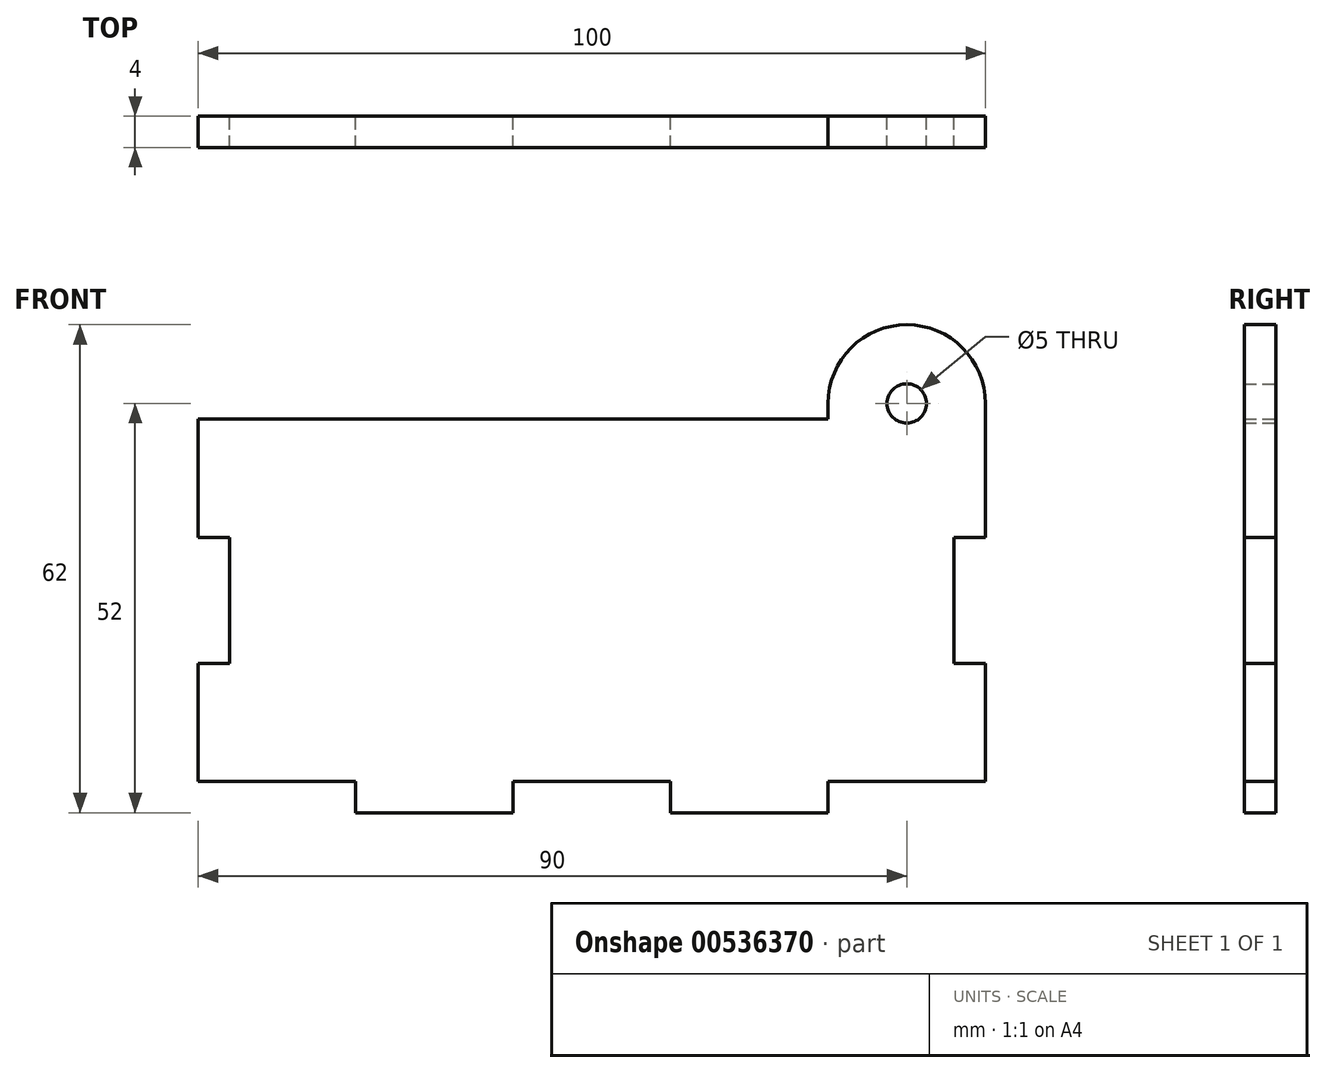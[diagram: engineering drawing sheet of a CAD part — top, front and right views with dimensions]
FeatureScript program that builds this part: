
annotation { "Feature Type Name" : "Feature", "Feature Type Description" : "" }
export const myFeature = defineFeature(function(context is Context, id is Id, definition is map)
    precondition{}
    {
        {
            var Q0;
            Q0=qCreatedBy(makeId("Front.planeOp"),FACE);
            var sketch = newSketch(context, id + "F0", { "sketchPlane" : qUnion([Q0])});
            skLineSegment(sketch, "E0.bottom", {"start": v(0, 0) * mm, "end": v(100, 0) * mm});
            skLineSegment(sketch, "E0.top", {"start": v(0, 50) * mm, "end": v(80, 50) * mm});
            skLineSegment(sketch, "E0.left", {"start": v(0, 0) * mm, "end": v(0, 50) * mm});
            skLineSegment(sketch, "E0.right", {"start": v(100, 0) * mm, "end": v(100, 50) * mm});
            skLineSegment(sketch, "E1.bottom", {"start": v(0, 0) * mm, "end": v(20, 0) * mm});
            skLineSegment(sketch, "E1.top", {"start": v(0, 4) * mm, "end": v(20, 4) * mm});
            skLineSegment(sketch, "E1.left", {"start": v(0, 0) * mm, "end": v(0, 4) * mm});
            skLineSegment(sketch, "E1.right", {"start": v(20, 0) * mm, "end": v(20, 4) * mm});
            skLineSegment(sketch, "E2.bottom", {"start": v(40, 0) * mm, "end": v(60, 0) * mm});
            skLineSegment(sketch, "E2.top", {"start": v(40, 4) * mm, "end": v(60, 4) * mm});
            skLineSegment(sketch, "E2.left", {"start": v(40, 0) * mm, "end": v(40, 4) * mm});
            skLineSegment(sketch, "E2.right", {"start": v(60, 0) * mm, "end": v(60, 4) * mm});
            skLineSegment(sketch, "E3.bottom", {"start": v(0, 35) * mm, "end": v(4, 35) * mm});
            skLineSegment(sketch, "E3.top", {"start": v(0, 19) * mm, "end": v(4, 19) * mm});
            skLineSegment(sketch, "E3.left", {"start": v(0, 35) * mm, "end": v(0, 19) * mm});
            skLineSegment(sketch, "E3.right", {"start": v(4, 35) * mm, "end": v(4, 19) * mm});
            skLineSegment(sketch, "E4.bottom", {"start": v(100, 35) * mm, "end": v(96, 35) * mm});
            skLineSegment(sketch, "E4.top", {"start": v(100, 19) * mm, "end": v(96, 19) * mm});
            skLineSegment(sketch, "E4.left", {"start": v(100, 35) * mm, "end": v(100, 19) * mm});
            skLineSegment(sketch, "E4.right", {"start": v(96, 35) * mm, "end": v(96, 19) * mm});
            skLineSegment(sketch, "E5.left", {"start": v(100, 50) * mm, "end": v(100, 52) * mm});
            skLineSegment(sketch, "E5.right", {"start": v(80, 50) * mm, "end": v(80, 52) * mm});
            skArc(sketch, "E6", {"start": v(100, 52) * mm, "mid": v(90, 62) * mm, "end": v(80, 52) * mm});
            skCircle(sketch, "E7", {"center": v(90, 52) * mm, "radius": 2.5 * mm});
            skLineSegment(sketch, "E8.bottom", {"start": v(100, 0) * mm, "end": v(80, 0) * mm});
            skLineSegment(sketch, "E8.top", {"start": v(100, 4) * mm, "end": v(80, 4) * mm});
            skLineSegment(sketch, "E8.left", {"start": v(100, 0) * mm, "end": v(100, 4) * mm});
            skLineSegment(sketch, "E8.right", {"start": v(80, 0) * mm, "end": v(80, 4) * mm});
            skSolve(sketch);
        }
        {
            var Q0;
            {var subQ2=sQuery(id+"F0.wireOp",EDGE,"E0.top");Q0=makeQuery(id+"F0.imprint","IMPRINT",FACE,{"disambiguationData":[TD([[makeQuery(id+"F0.imprint","IMPRINT",EDGE,{"derivedFrom":subQ2}),-1.0]])]});}
            extrude(context, id + "F1", {"entities" : qUnion([Q0]), "depth" : 4 * mm, "offsetDistance" : 25 * mm});
        }
    });
